# Revit family: R 3-1500 (a)
name_source: partatom
category: Equipement spécialisé
revit_build: Autodesk Revit LT 2015 (Build: 20140606_1530(x64)
units: mm (PartAtom-declared; Revit-internal decimal feet)

## types (4) — shared parameters
Apparent Power = 0 VA
Depth = 302 mm
Description = CUTTERS DE TABLE
Electrique connexion = 40 mm  [stored 0.131234 ft]
Fabricant = ROBOT COUPE
Height = 425 mm
Modèle = R 3-1500
Phase = 1
Speeds (Rpm) = 1500
URL = www.robot-coupe.com
Watts = 650 W
Weight = 11.2 kg
Width = 283 mm
water = Connector
zero-valued in all types: Cold water supply, Cold water supply height, Top, Used water, Waste water height

## per-type parameters (varying)
| type | Amps | Cycle | Volts |
| R 3-1500    230/50/1 | 5.7 A | 50 Hz | 230 V |
| R 3-1500    120/60/1 | 12 A | 60 Hz | 120 V |
| R 3-1500    220/60/1 | 5.7 A | 60 Hz | 220 V |
| R 3-1500    220-240/50/1 | 5.7 A | 50 Hz | 220 V |

note: [stored X ft] marks values corroborated as IEEE doubles in the binary element streams (Revit-internal decimal feet)

## geometry (parser evidence)
native form markers: Blend x104, Sweep x4
no freeform markers — native parametric forms only
